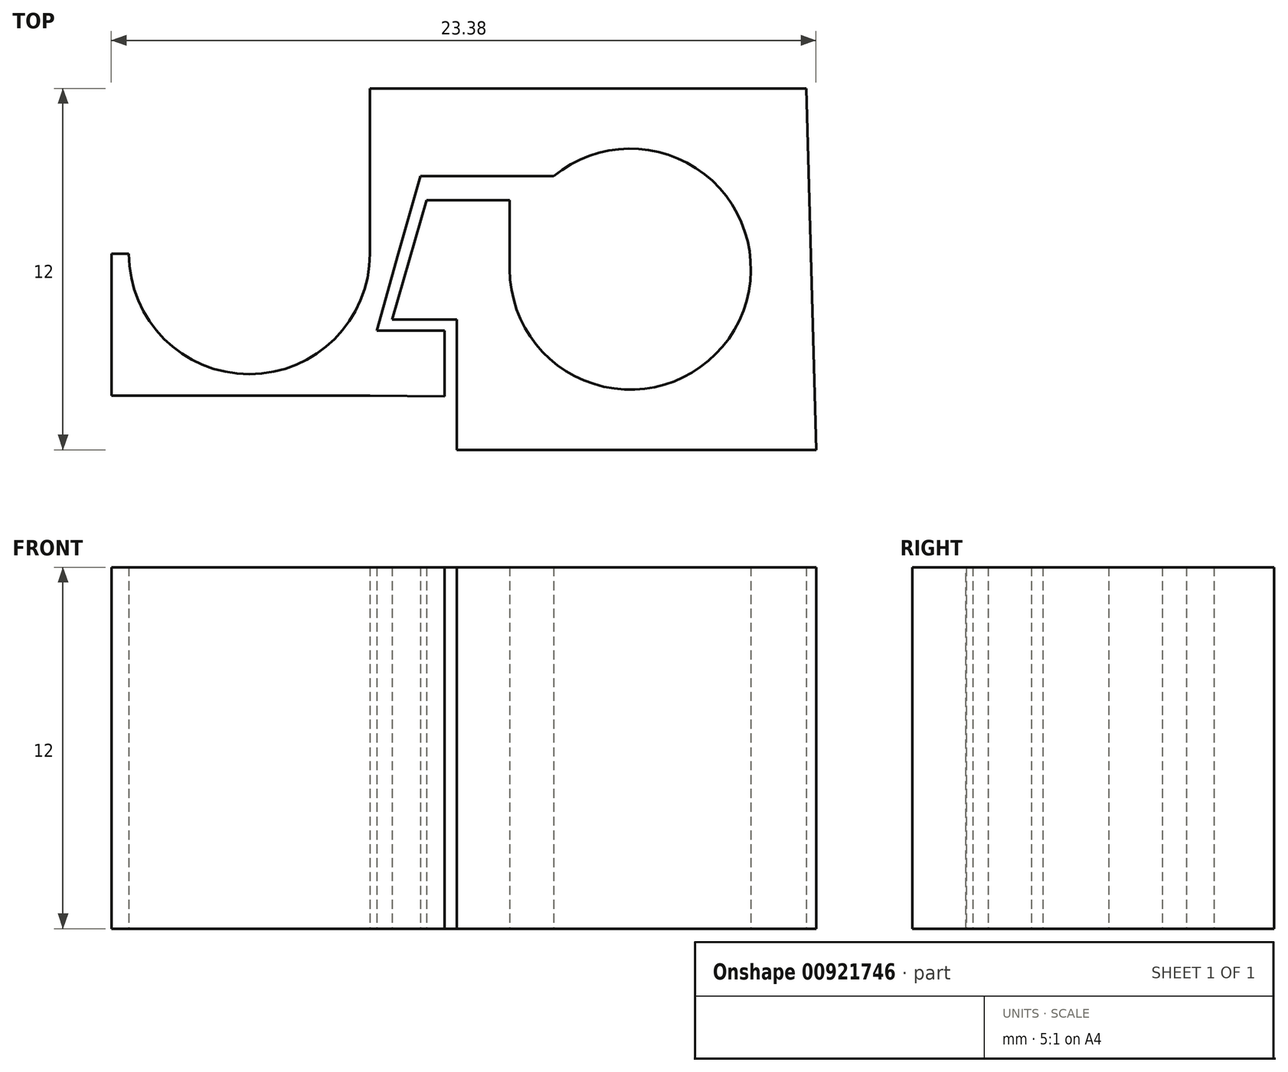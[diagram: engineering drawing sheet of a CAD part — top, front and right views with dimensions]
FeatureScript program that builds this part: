
annotation { "Feature Type Name" : "Feature", "Feature Type Description" : "" }
export const myFeature = defineFeature(function(context is Context, id is Id, definition is map)
    precondition{}
    {
        {
            var Q0;
            Q0=qCreatedBy(makeId("Top.planeOp"),FACE);
            var sketch = newSketch(context, id + "F0", { "sketchPlane" : qUnion([Q0])});
            skArc(sketch, "E0", {"start": v(-4, 0) * mm, "mid": v(3.62, -1.7) * mm, "end": v(-2.54, 3.09) * mm});
            skCircle(sketch, "E1.0", {"center": v(0, 0) * mm, "radius": 6 * mm, "construction": true});
            skLineSegment(sketch, "E2", {"start": v(5.84, 6) * mm, "end": v(6.16, -6) * mm});
            skLineSegment(sketch, "E3", {"start": v(6.16, -6) * mm, "end": v(-5.76, -6) * mm});
            skLineSegment(sketch, "E4", {"start": v(5.84, 6) * mm, "end": v(-8.64, 6) * mm});
            skPoint(sketch, "E5.endSnap0", {"position": v(-5.76, -5) * mm});
            skLineSegment(sketch, "E6", {"start": v(-7.9, -1.67) * mm, "end": v(-6.76, 2.29) * mm});
            skLineSegment(sketch, "E7", {"start": v(-6.76, 2.29) * mm, "end": v(-4, 2.29) * mm});
            skLineSegment(sketch, "E8", {"start": v(-4, 2.29) * mm, "end": v(-4, 0) * mm});
            skLineSegment(sketch, "E9", {"start": v(-7.7, 0.51) * mm, "end": v(-8.41, -2.05) * mm});
            skLineSegment(sketch, "E10", {"start": v(-6.15, -4.23) * mm, "end": v(-8.64, -4.2) * mm});
            skLineSegment(sketch, "E11", {"start": v(-8.64, 6) * mm, "end": v(-8.64, 0.51) * mm});
            skLineSegment(sketch, "E12", {"start": v(-8.64, 6) * mm, "end": v(-8.64, 6) * mm});
            skLineSegment(sketch, "E13", {"start": v(-5.76, -6) * mm, "end": v(-5.76, -1.67) * mm});
            skLineSegment(sketch, "E14", {"start": v(-5.76, -1.67) * mm, "end": v(-7.9, -1.67) * mm});
            skLineSegment(sketch, "E15", {"start": v(-8.41, -2.05) * mm, "end": v(-6.17, -2.05) * mm});
            skLineSegment(sketch, "E16", {"start": v(-6.17, -2.05) * mm, "end": v(-6.17, -4.23) * mm});
            skLineSegment(sketch, "E17", {"start": v(-8.64, -4.2) * mm, "end": v(-17.22, -4.2) * mm});
            skLineSegment(sketch, "E18", {"start": v(-17.22, -4.2) * mm, "end": v(-17.22, 0.51) * mm});
            skLineSegment(sketch, "E19", {"start": v(-17.22, 0.51) * mm, "end": v(-16.64, 0.51) * mm});
            skArc(sketch, "E20", {"start": v(-16.64, 0.51) * mm, "mid": v(-12.64, -3.49) * mm, "end": v(-8.64, 0.51) * mm});
            skPoint(sketch, "E21", {"position": v(-12.64, -3.49) * mm});
            skLineSegment(sketch, "E22", {"start": v(-7.7, 0.51) * mm, "end": v(-6.96, 3.09) * mm});
            skLineSegment(sketch, "E23", {"start": v(-6.96, 3.09) * mm, "end": v(-2.54, 3.09) * mm});
            skSolve(sketch);
        }
        {
            var Q0;
            Q0 = qSketchRegion(id + "F0", true);
            extrude(context, id + "F1", {"entities" : qUnion([Q0]), "depth" : 12 * mm, "offsetDistance" : 25 * mm});
        }
    });
